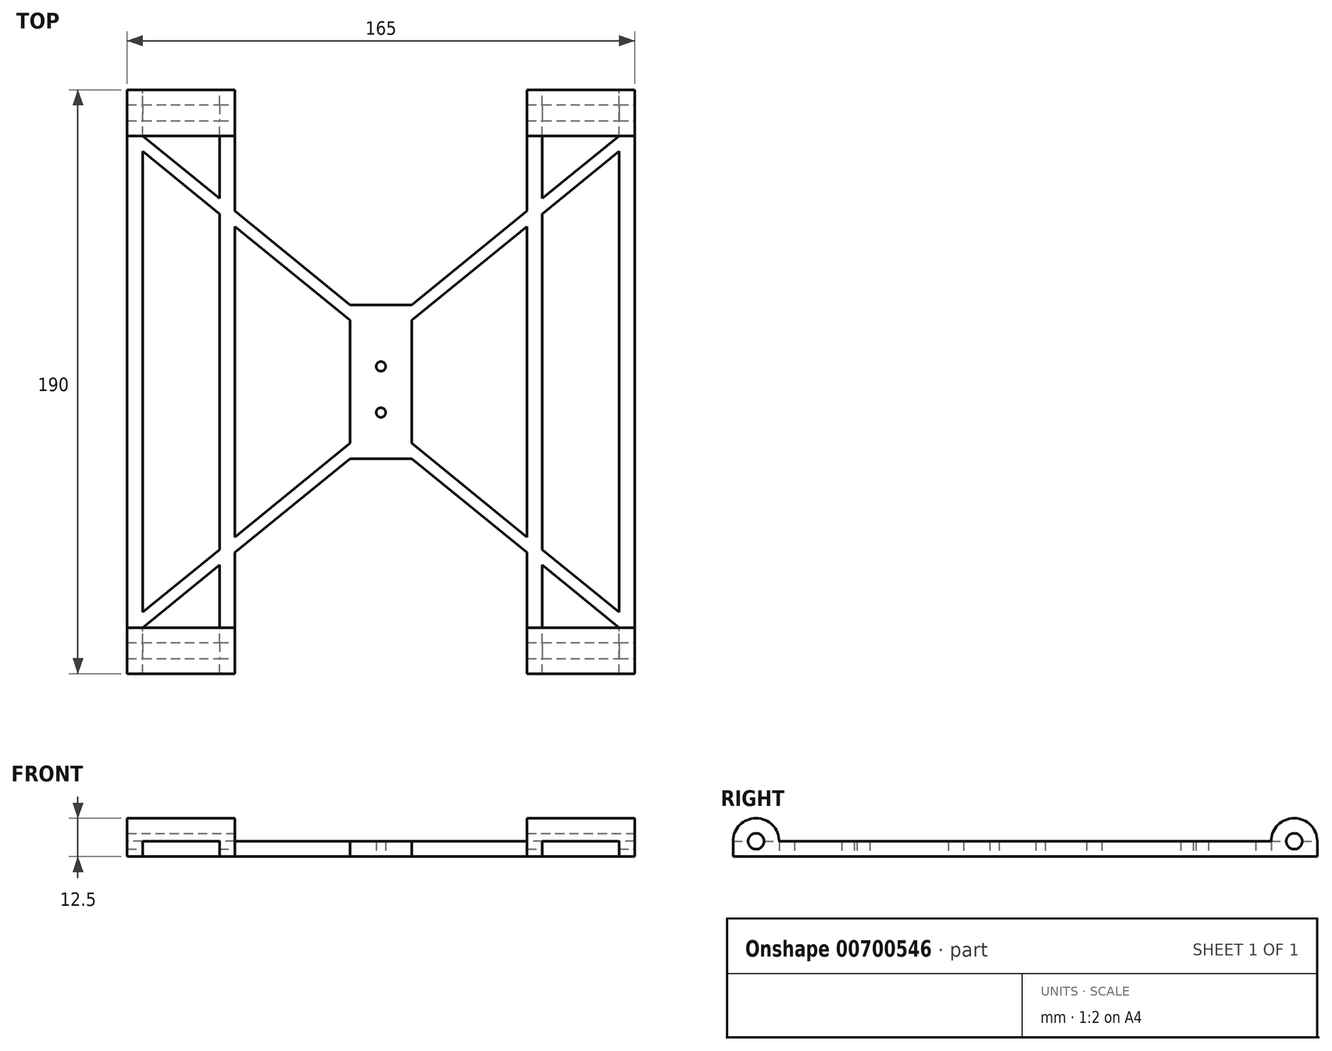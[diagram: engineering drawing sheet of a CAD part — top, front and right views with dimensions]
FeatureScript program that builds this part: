
annotation { "Feature Type Name" : "Feature", "Feature Type Description" : "" }
export const myFeature = defineFeature(function(context is Context, id is Id, definition is map)
    precondition{}
    {
        {
            var Q0;
            Q0=qCreatedBy(makeId("Top.planeOp"),FACE);
            var sketch = newSketch(context, id + "F0", { "sketchPlane" : qUnion([Q0])});
            skLineSegment(sketch, "E0.bottom", {"start": v(10, -25) * mm, "end": v(-10, -25) * mm});
            skLineSegment(sketch, "E0.top", {"start": v(10, 25) * mm, "end": v(-10, 25) * mm});
            skLineSegment(sketch, "E0.left", {"start": v(10, -25) * mm, "end": v(10, 25) * mm});
            skLineSegment(sketch, "E0.right", {"start": v(-10, -25) * mm, "end": v(-10, 25) * mm});
            skPoint(sketch, "E0.middle", {"position": v(0, 0) * mm});
            skLineSegment(sketch, "E1.bottom", {"start": v(-77.5, -95) * mm, "end": v(-82.5, -95) * mm});
            skLineSegment(sketch, "E1.top", {"start": v(-77.5, 95) * mm, "end": v(-82.5, 95) * mm});
            skLineSegment(sketch, "E1.left", {"start": v(-77.5, -95) * mm, "end": v(-77.5, 95) * mm});
            skLineSegment(sketch, "E1.right", {"start": v(-82.5, -95) * mm, "end": v(-82.5, 95) * mm});
            skPoint(sketch, "E1.middle", {"position": v(-80, 0) * mm});
            skLineSegment(sketch, "E2.bottom", {"start": v(82.5, -95) * mm, "end": v(77.5, -95) * mm});
            skLineSegment(sketch, "E2.top", {"start": v(82.5, 95) * mm, "end": v(77.5, 95) * mm});
            skLineSegment(sketch, "E2.left", {"start": v(82.5, -95) * mm, "end": v(82.5, 95) * mm});
            skLineSegment(sketch, "E2.right", {"start": v(77.5, -95) * mm, "end": v(77.5, 95) * mm});
            skPoint(sketch, "E2.middle", {"position": v(80, 0) * mm});
            skPoint(sketch, "E2.middle.positionSnap0", {"position": v(-10, 0) * mm});
            skPoint(sketch, "E2.centerSnap0", {"position": v(-10, 0) * mm});
            skLineSegment(sketch, "E3.bottom", {"start": v(-47.5, -95) * mm, "end": v(-52.5, -95) * mm});
            skLineSegment(sketch, "E3.top", {"start": v(-47.5, 95) * mm, "end": v(-52.5, 95) * mm});
            skLineSegment(sketch, "E3.left", {"start": v(-47.5, -95) * mm, "end": v(-47.5, 95) * mm});
            skLineSegment(sketch, "E3.right", {"start": v(-52.5, -95) * mm, "end": v(-52.5, 95) * mm});
            skPoint(sketch, "E3.middle", {"position": v(-50, 0) * mm});
            skLineSegment(sketch, "E4.bottom", {"start": v(52.5, -95) * mm, "end": v(47.5, -95) * mm});
            skLineSegment(sketch, "E4.top", {"start": v(52.5, 95) * mm, "end": v(47.5, 95) * mm});
            skLineSegment(sketch, "E4.left", {"start": v(52.5, -95) * mm, "end": v(52.5, 95) * mm});
            skLineSegment(sketch, "E4.right", {"start": v(47.5, -95) * mm, "end": v(47.5, 95) * mm});
            skPoint(sketch, "E4.middle", {"position": v(50, 0) * mm});
            skCircle(sketch, "E5", {"center": v(0, 5) * mm, "radius": 1.55 * mm});
            skCircle(sketch, "E6", {"center": v(0, -10) * mm, "radius": 1.55 * mm});
            skLineSegment(sketch, "E7", {"start": v(-77.5, 80) * mm, "end": v(-10, 25) * mm});
            skLineSegment(sketch, "E8", {"start": v(-77.5, 75) * mm, "end": v(-10, 20) * mm});
            skLineSegment(sketch, "E9", {"start": v(10, 25) * mm, "end": v(77.5, 80) * mm});
            skLineSegment(sketch, "E10", {"start": v(10, 20) * mm, "end": v(77.5, 75) * mm});
            skLineSegment(sketch, "E11", {"start": v(-10, -25) * mm, "end": v(-77.5, -80) * mm});
            skLineSegment(sketch, "E12", {"start": v(-10, -20) * mm, "end": v(-77.5, -75) * mm});
            skLineSegment(sketch, "E13", {"start": v(10, -25) * mm, "end": v(77.5, -80) * mm});
            skLineSegment(sketch, "E14", {"start": v(77.5, -75) * mm, "end": v(10, -20) * mm});
            skPoint(sketch, "E15", {"position": v(-52.5, 59.63) * mm});
            skSolve(sketch);
        }
        {
            var Q0;
            Q0 = qSketchRegion(id + "F0", true);
            var Q1;
            {var subQ0=sQuery(id+"F0.wireOp",EDGE,"E12");var subQ1=sQuery(id+"F0.wireOp",EDGE,"E3.left");var subQ2=makeQuery(id+"F0.imprint","INTERSECT",VERTEX,{"derivedFrom":[subQ1,subQ0]});Q1=makeQuery(id+"F0.imprint","IMPRINT",FACE,{"disambiguationData":[TD([[makeQuery(id+"F0.imprint","IMPRINT",EDGE,{"disambiguationData":[TD([[subQ2,-1.0]])],"derivedFrom":subQ1}),1.0]])]});}
            var Q2;
            {var subQ0=sQuery(id+"F0.wireOp",EDGE,"E14");var subQ1=sQuery(id+"F0.wireOp",EDGE,"E4.left");var subQ2=makeQuery(id+"F0.imprint","INTERSECT",VERTEX,{"derivedFrom":[subQ1,subQ0]});Q2=makeQuery(id+"F0.imprint","IMPRINT",FACE,{"disambiguationData":[TD([[makeQuery(id+"F0.imprint","IMPRINT",EDGE,{"disambiguationData":[TD([[subQ2,-1.0]])],"derivedFrom":subQ1}),1.0]])]});}
            extrude(context, id + "F1", {"entities" : qUnion([Q0, Q1, Q2]), "depth" : 5 * mm, "offsetDistance" : 25 * mm});
        }
        {
            var Q0;
            Q0=makeQuery(id+"F1.opExtrude","SWEPT_FACE",FACE,{"disambiguationData":[OSD([sQuery(id+"F0.wireOp",EDGE,"E1.right")])]});
            var sketch = newSketch(context, id + "F2", { "sketchPlane" : qUnion([Q0])});
            skArc(sketch, "E16", {"start": v(-80, 5) * mm, "mid": v(-87.5, 12.5) * mm, "end": v(-95, 5) * mm});
            skLineSegment(sketch, "E17", {"start": v(-95, 5) * mm, "end": v(-80, 5) * mm});
            skArc(sketch, "E18", {"start": v(95, 5) * mm, "mid": v(87.5, 12.5) * mm, "end": v(80, 5) * mm});
            skLineSegment(sketch, "E19", {"start": v(80, 5) * mm, "end": v(95, 5) * mm});
            skSolve(sketch);
        }
        {
            var Q0;
            Q0 = qSketchRegion(id + "F2", true);
            var Q1;
            Q1=makeQuery(id+"F1.opExtrude","SWEPT_FACE",FACE,{"disambiguationData":[OSD([sQuery(id+"F0.wireOp",EDGE,"E2.left")])]});
            extrude(context, id + "F3", {"entities" : qUnion([Q0]), "operationType" : NewBodyOperationType.ADD, "endBound" : BoundingType.UP_TO_SURFACE, "oppositeDirection" : true, "depth" : 25 * mm, "endBoundEntityFace" : qUnion([Q1]), "offsetDistance" : 25 * mm});
        }
        {
            var Q0;
            {var subQ0=sQuery(id+"F0.wireOp",EDGE,"E2.top");Q0=makeQuery(id+"F3.boolean.opBoolean","SPLIT",FACE,{"disambiguationData":[TD([makeQuery(id+"F1.opExtrude","SWEPT_FACE",FACE,{"disambiguationData":[OSD([subQ0])]})])],"derivedFrom":makeQuery(id+"F3.opExtrude","SWEPT_FACE",FACE,{"disambiguationData":[OSD([sQuery(id+"F2.wireOp",EDGE,"E17")])]})});}
            var Q1;
            {var subQ0=sQuery(id+"F0.wireOp",EDGE,"E3.top");var subQ2=sQuery(id+"F0.wireOp",EDGE,"E3.left");Q1=makeQuery(id+"F3.boolean.opBoolean","SPLIT",FACE,{"disambiguationData":[TD([makeQuery(id+"F1.opExtrude","SWEPT_FACE",FACE,{"disambiguationData":[OSD([subQ2]),TDD([makeQuery(id+"F0.imprint","IMPRINT",EDGE,{"disambiguationData":[TD([[makeQuery(id+"F0.imprint","INTERSECT",VERTEX,{"derivedFrom":[subQ0,subQ2]}),1.0]])],"derivedFrom":subQ2})])]})])],"derivedFrom":makeQuery(id+"F3.opExtrude","SWEPT_FACE",FACE,{"disambiguationData":[OSD([sQuery(id+"F2.wireOp",EDGE,"E17")])]})});}
            var Q2;
            {var subQ2=sQuery(id+"F0.wireOp",EDGE,"E1.top");Q2=makeQuery(id+"F3.boolean.opBoolean","SPLIT",FACE,{"disambiguationData":[TD([makeQuery(id+"F1.opExtrude","SWEPT_FACE",FACE,{"disambiguationData":[OSD([subQ2])]})])],"derivedFrom":makeQuery(id+"F3.opExtrude","SWEPT_FACE",FACE,{"disambiguationData":[OSD([sQuery(id+"F2.wireOp",EDGE,"E17")])]})});}
            var Q3;
            {var subQ2=sQuery(id+"F0.wireOp",EDGE,"E1.bottom");Q3=makeQuery(id+"F3.boolean.opBoolean","SPLIT",FACE,{"disambiguationData":[TD([makeQuery(id+"F1.opExtrude","SWEPT_FACE",FACE,{"disambiguationData":[OSD([subQ2])]})])],"derivedFrom":makeQuery(id+"F3.opExtrude","SWEPT_FACE",FACE,{"disambiguationData":[OSD([sQuery(id+"F2.wireOp",EDGE,"E19")])]})});}
            var Q4;
            {var subQ1=sQuery(id+"F0.wireOp",EDGE,"E3.left");var subQ2=sQuery(id+"F0.wireOp",EDGE,"E3.bottom");Q4=makeQuery(id+"F3.boolean.opBoolean","SPLIT",FACE,{"disambiguationData":[TD([makeQuery(id+"F1.opExtrude","SWEPT_FACE",FACE,{"disambiguationData":[OSD([subQ1]),TDD([makeQuery(id+"F0.imprint","IMPRINT",EDGE,{"disambiguationData":[TD([[makeQuery(id+"F0.imprint","INTERSECT",VERTEX,{"derivedFrom":[subQ2,subQ1]}),-1.0]])],"derivedFrom":subQ1})])]})])],"derivedFrom":makeQuery(id+"F3.opExtrude","SWEPT_FACE",FACE,{"disambiguationData":[OSD([sQuery(id+"F2.wireOp",EDGE,"E19")])]})});}
            var Q5;
            {var subQ2=sQuery(id+"F0.wireOp",EDGE,"E2.bottom");Q5=makeQuery(id+"F3.boolean.opBoolean","SPLIT",FACE,{"disambiguationData":[TD([makeQuery(id+"F1.opExtrude","SWEPT_FACE",FACE,{"disambiguationData":[OSD([subQ2])]})])],"derivedFrom":makeQuery(id+"F3.opExtrude","SWEPT_FACE",FACE,{"disambiguationData":[OSD([sQuery(id+"F2.wireOp",EDGE,"E19")])]})});}
            extrude(context, id + "F4", {"entities" : qUnion([Q0, Q1, Q2, Q3, Q4, Q5]), "operationType" : NewBodyOperationType.REMOVE, "oppositeDirection" : true, "depth" : 25 * mm, "offsetDistance" : 25 * mm});
        }
        {
            var Q0;
            {var subQ0=sQuery(id+"F0.wireOp",EDGE,"E2.left");Q0=makeQuery(id+"F3.boolean.opBoolean","MERGE",FACE,{"derivedFrom":[makeQuery(id+"F1.opExtrude","SWEPT_FACE",FACE,{"disambiguationData":[OSD([subQ0])]}),makeQuery(id+"F3.opExtrude","CAP_FACE",FACE,{"disambiguationData":[OSD([subQ0]),OD(0.0)],"isStart":false}),makeQuery(id+"F3.opExtrude","CAP_FACE",FACE,{"disambiguationData":[OSD([subQ0]),OD(1.0)],"isStart":false})]});}
            var sketch = newSketch(context, id + "F5", { "sketchPlane" : qUnion([Q0])});
            skCircle(sketch, "E20", {"center": v(-87.5, 5) * mm, "radius": 2.6 * mm});
            skCircle(sketch, "E21", {"center": v(87.5, 5) * mm, "radius": 2.6 * mm});
            skSolve(sketch);
        }
        {
            var Q0;
            Q0 = qSketchRegion(id + "F5", true);
            extrude(context, id + "F6", {"entities" : qUnion([Q0]), "operationType" : NewBodyOperationType.REMOVE, "endBound" : BoundingType.THROUGH_ALL, "oppositeDirection" : true, "depth" : 25 * mm, "offsetDistance" : 25 * mm});
        }
    });
